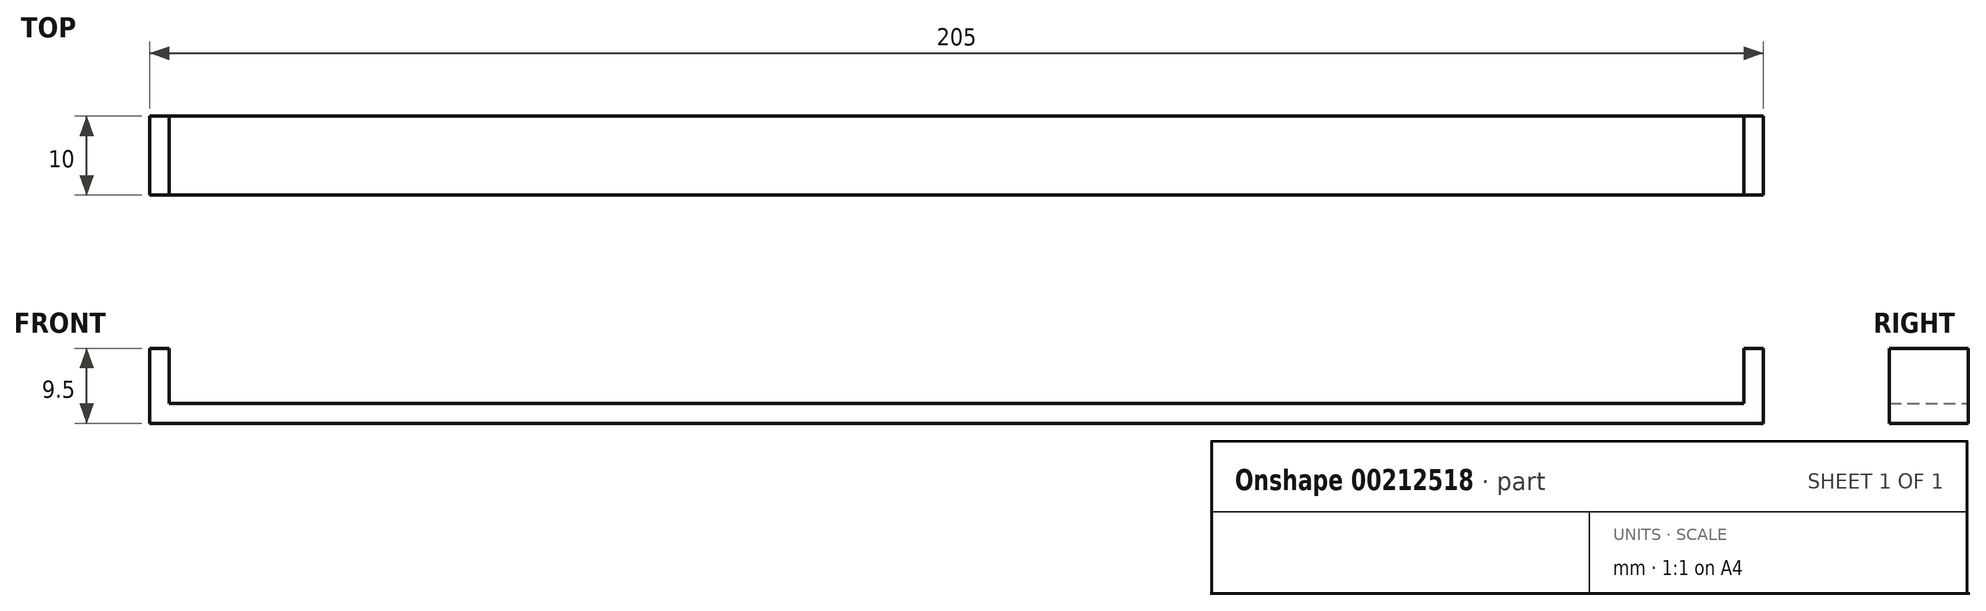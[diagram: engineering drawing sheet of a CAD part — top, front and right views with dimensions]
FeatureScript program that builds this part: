
annotation { "Feature Type Name" : "Feature", "Feature Type Description" : "" }
export const myFeature = defineFeature(function(context is Context, id is Id, definition is map)
    precondition{}
    {
        {
            var Q0;
            Q0=qCreatedBy(makeId("Front.planeOp"),FACE);
            var sketch = newSketch(context, id + "F0", { "sketchPlane" : qUnion([Q0])});
            skLineSegment(sketch, "E0", {"start": v(0, 0) * mm, "end": v(100, 0) * mm});
            skLineSegment(sketch, "E1", {"start": v(100, 0) * mm, "end": v(100, 7) * mm});
            skLineSegment(sketch, "E2", {"start": v(100, 7) * mm, "end": v(102.5, 7) * mm});
            skLineSegment(sketch, "E3.0", {"start": v(102.5, -2.5) * mm, "end": v(102.5, 7) * mm});
            skLineSegment(sketch, "E4.0", {"start": v(0, -2.5) * mm, "end": v(102.5, -2.5) * mm});
            skLineSegment(sketch, "E5", {"start": v(0, 0) * mm, "end": v(0, -16.8) * mm, "construction": true});
            skLineSegment(sketch, "E6.MirrorCS", {"start": v(-100, 7) * mm, "end": v(-102.5, 7) * mm});
            skLineSegment(sketch, "E7.MirrorCS", {"start": v(-100, 0) * mm, "end": v(-100, 7) * mm});
            skLineSegment(sketch, "E8.MirrorCS", {"start": v(-102.5, -2.5) * mm, "end": v(-102.5, 7) * mm});
            skLineSegment(sketch, "E9.MirrorCS", {"start": v(0, 0) * mm, "end": v(-100, 0) * mm});
            skLineSegment(sketch, "E10.MirrorCS", {"start": v(0, -2.5) * mm, "end": v(-102.5, -2.5) * mm});
            skSolve(sketch);
        }
        {
            var Q0;
            Q0=makeQuery(id+"F0.imprint","IMPRINT",FACE,{"disambiguationData":[TD([[makeQuery(id+"F0.imprint","IMPRINT",EDGE,{"derivedFrom":sQuery(id+"F0.wireOp",EDGE,"E0")}),-1.0]])]});
            extrude(context, id + "F1", {"entities" : qUnion([Q0]), "endBound" : BoundingType.SYMMETRIC, "depth" : 10 * mm});
        }
    });
